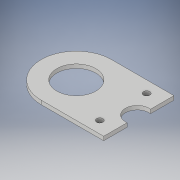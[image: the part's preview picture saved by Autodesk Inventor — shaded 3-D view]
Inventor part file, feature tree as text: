
AUTODESK INVENTOR PART (.ipt)
format: ipt  version: 2019 (Build 230136000, 136)  size: 118,784 bytes
history: native  units: in
note: dims shown in document units (in); Inventor stores cm internally (conversion verified against a paired STEP export)
features: extrude x1, sketch x1
ambient origin geometry x8: Origin, YZ Plane, XZ Plane, XY Plane, X Axis, Y Axis, Z Axis, Center Point
bodies: Solid1 (feature_tree)
feature tree (2):
  extrude  "Extrusion1"  Depth=0.125in
  sketch  "Sketch1"  dims[d0=1.25in d1=0.5in d2=2.0in d3=0.75in d4=0.75in d5=0.5in d6=2.0in d7=0.75in d8=0.75in d9=0.2031in d10=0.2031in d11=0.125in d12=0.0in]
